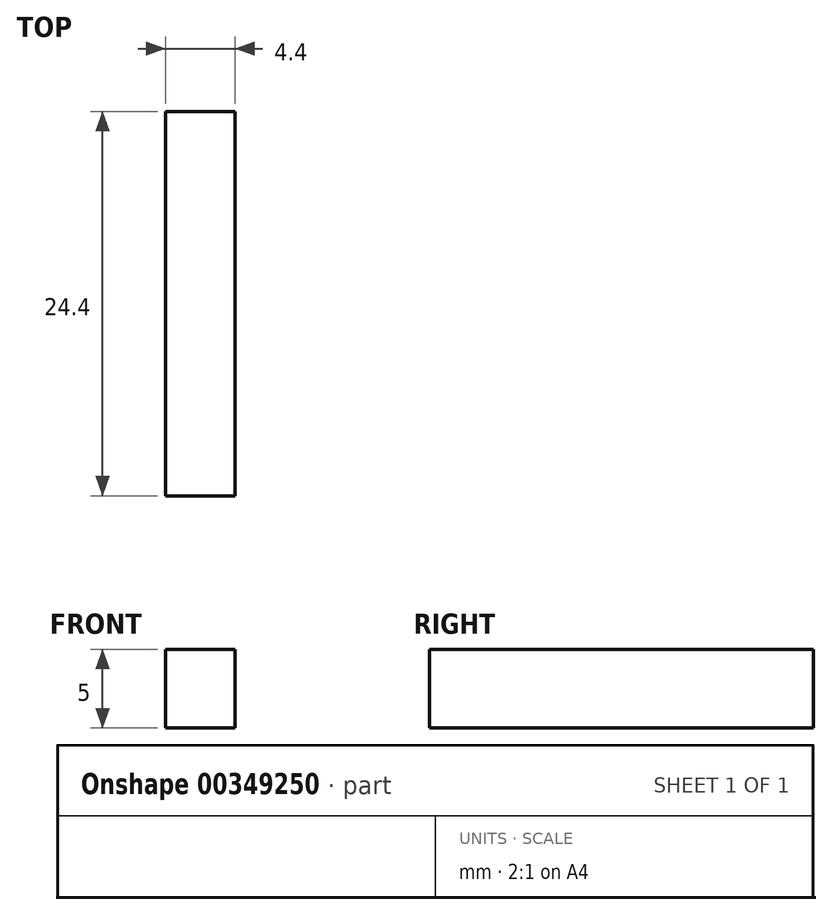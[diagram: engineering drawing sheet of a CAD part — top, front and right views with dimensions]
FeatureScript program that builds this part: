
annotation { "Feature Type Name" : "Feature", "Feature Type Description" : "" }
export const myFeature = defineFeature(function(context is Context, id is Id, definition is map)
    precondition{}
    {
        {
            var Q0;
            Q0=qCreatedBy(makeId("Top.planeOp"),FACE);
            var sketch = newSketch(context, id + "F0", { "sketchPlane" : qUnion([Q0])});
            skLineSegment(sketch, "E0.bottom", {"start": v(0, 0) * mm, "end": v(-4.4, 0) * mm});
            skLineSegment(sketch, "E0.top", {"start": v(0, -24.4) * mm, "end": v(-4.4, -24.4) * mm});
            skLineSegment(sketch, "E0.left", {"start": v(0, 0) * mm, "end": v(0, -24.4) * mm});
            skLineSegment(sketch, "E0.right", {"start": v(-4.4, 0) * mm, "end": v(-4.4, -24.4) * mm});
            skSolve(sketch);
        }
        {
            var Q0;
            Q0=qSketchRegion(id+"F0",true);
            extrude(context, id + "F1", {"entities" : qUnion([Q0]), "depth" : 5 * mm});
        }
    });
